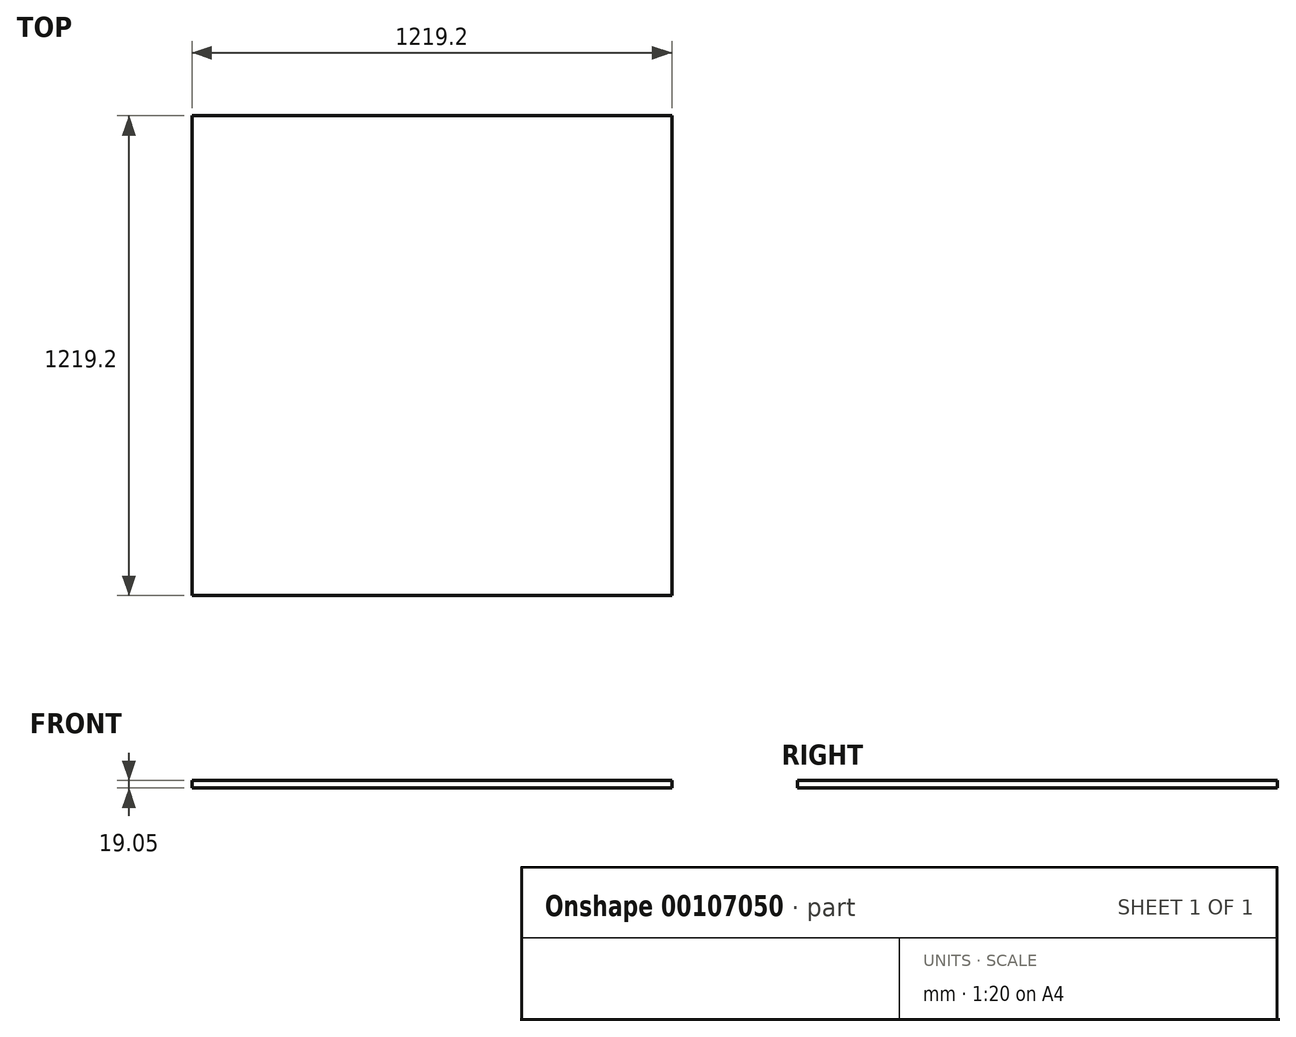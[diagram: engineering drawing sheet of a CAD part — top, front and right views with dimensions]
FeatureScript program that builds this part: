
annotation { "Feature Type Name" : "Feature", "Feature Type Description" : "" }
export const myFeature = defineFeature(function(context is Context, id is Id, definition is map)
    precondition{}
    {
        {
            var Q0;
            Q0=qCreatedBy(makeId("Top.planeOp"),FACE);
            var sketch = newSketch(context, id + "F0", { "sketchPlane" : qUnion([Q0])});
            skLineSegment(sketch, "E0.bottom", {"start": v(-1151.03, 1159.07) * mm, "end": v(68.17, 1159.07) * mm});
            skLineSegment(sketch, "E0.top", {"start": v(-1151.03, -60.13) * mm, "end": v(68.17, -60.13) * mm});
            skLineSegment(sketch, "E0.left", {"start": v(-1151.03, 1159.07) * mm, "end": v(-1151.03, -60.13) * mm});
            skLineSegment(sketch, "E0.right", {"start": v(68.17, 1159.07) * mm, "end": v(68.17, -60.13) * mm});
            skSolve(sketch);
        }
        {
            var Q0;
            Q0=makeQuery(id+"F0.imprint","IMPRINT",FACE,{"disambiguationData":[TD([[makeQuery(id+"F0.imprint","IMPRINT",EDGE,{"derivedFrom":sQuery(id+"F0.wireOp",EDGE,"E0.bottom")}),-1.0]])]});
            extrude(context, id + "F1", {"entities" : qUnion([Q0]), "depth" : 19.05 * mm});
        }
    });
